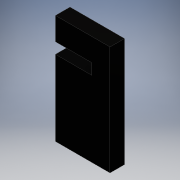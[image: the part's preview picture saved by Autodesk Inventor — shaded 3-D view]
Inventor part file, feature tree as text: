
AUTODESK INVENTOR PART (.ipt)
format: ipt  version: 2016 (Build 200138000, 138)  size: 94,720 bytes
history: native  units: mm
features: extrude x1, sketch x1
ambient origin geometry x8: Origin, YZ Plane, XZ Plane, XY Plane, X Axis, Y Axis, Z Axis, Center Point
bodies: Solid1 (feature_tree)
feature tree (2):
  extrude  "Extrusion1"  Depth=30.0mm
  sketch  "Sketch1"  dims[d0=15.0mm d1=30.0mm d2=10.0mm d3=20.75mm d4=4.0mm d5=0.0mm d6=3.0mm]
